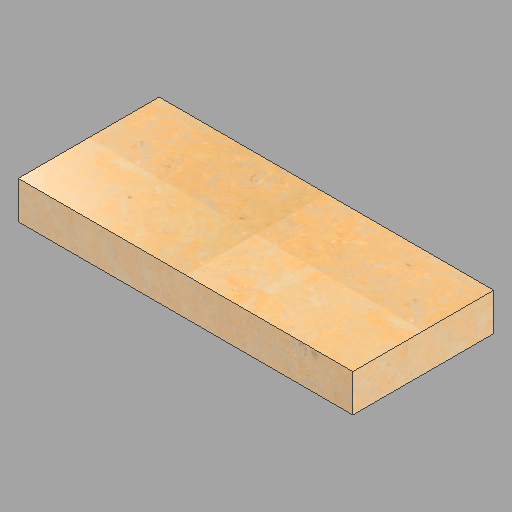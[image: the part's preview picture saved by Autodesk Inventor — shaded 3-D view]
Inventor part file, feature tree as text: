
AUTODESK INVENTOR PART (.ipt)
format: ipt  version: 2023 (Build 270158030, 158C)  size: 251,904 bytes
history: native  units: in
note: dims shown in document units (in); Inventor stores cm internally (conversion verified against a paired STEP export)
features: extrude x1, sketch x1
ambient origin geometry x8: Origin, YZ Plane, XZ Plane, XY Plane, X Axis, Y Axis, Z Axis, Center Point
bodies: Solid1 (feature_tree)
feature tree (2):
  extrude  "Extrusion1"  Depth=15.0in
  sketch  "Sketch1"  dims[d0=35.625in d1=15.0in d2=4.0in d3=0.0in]
